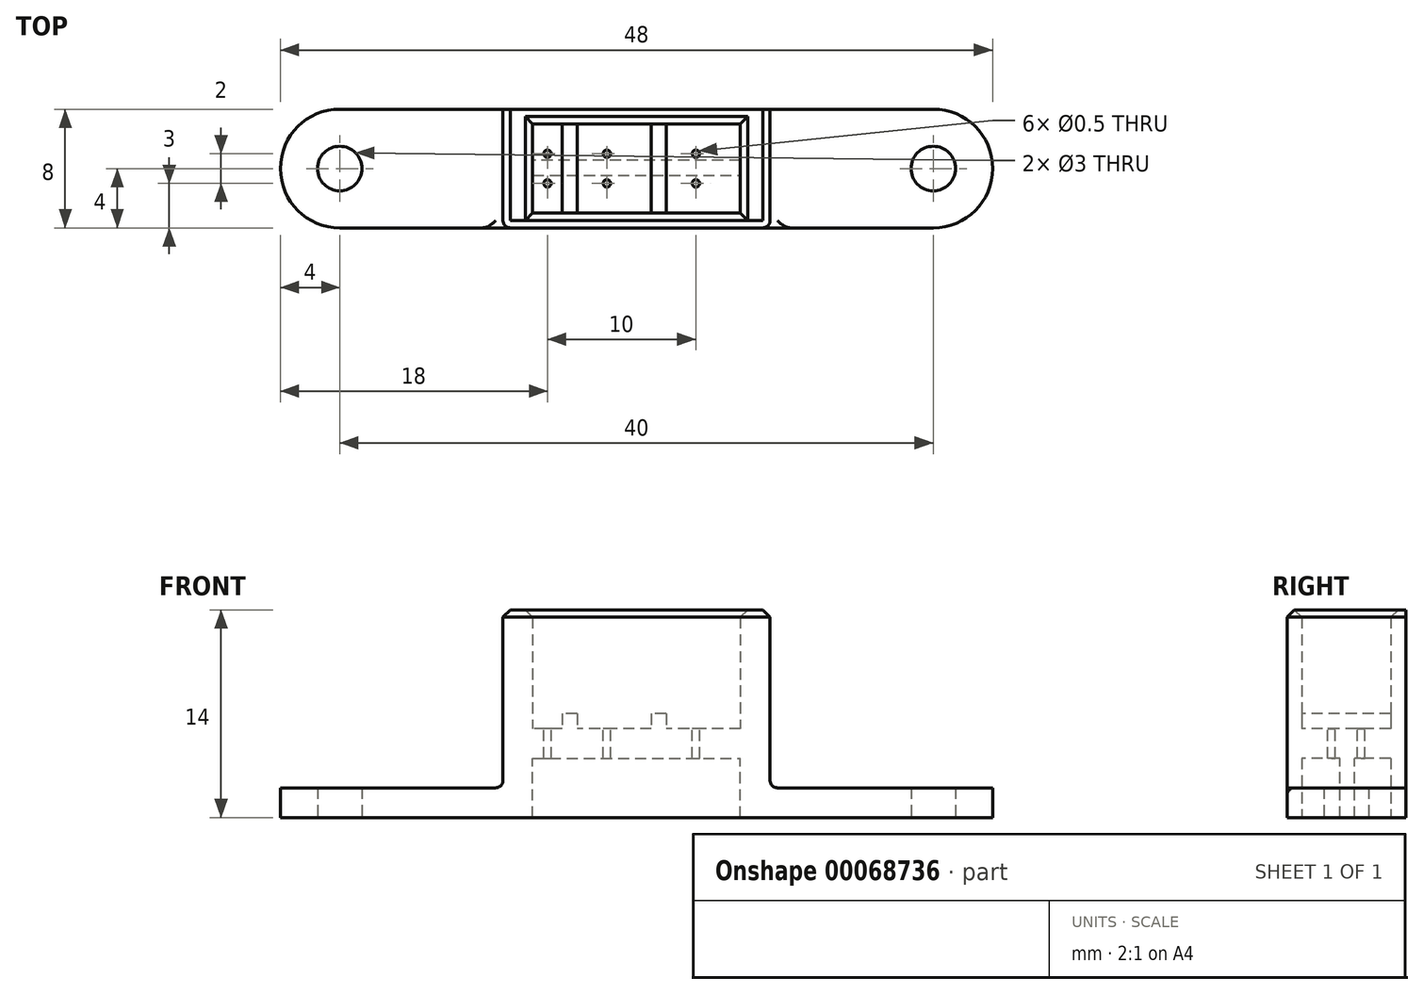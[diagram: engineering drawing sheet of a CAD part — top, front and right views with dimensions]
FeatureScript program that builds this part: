
annotation { "Feature Type Name" : "Feature", "Feature Type Description" : "" }
export const myFeature = defineFeature(function(context is Context, id is Id, definition is map)
    precondition{}
    {
        {
            var Q0;
            Q0=qCreatedBy(makeId("Top.planeOp"),FACE);
            var sketch = newSketch(context, id + "F0", { "sketchPlane" : qUnion([Q0])});
            skCircle(sketch, "E0", {"center": v(20, 0) * mm, "radius": 1.5 * mm});
            skLineSegment(sketch, "E1", {"start": v(20, 0) * mm, "end": v(0, 0) * mm, "construction": true});
            skLineSegment(sketch, "E2", {"start": v(0, 4) * mm, "end": v(20, 4) * mm});
            skLineSegment(sketch, "E3", {"start": v(0, -4) * mm, "end": v(20, -4) * mm});
            skArc(sketch, "E4", {"start": v(20, -4) * mm, "mid": v(24, 0) * mm, "end": v(20, 4) * mm});
            skLineSegment(sketch, "E5", {"start": v(0, 4) * mm, "end": v(0, -4) * mm, "construction": true});
            skLineSegment(sketch, "E6.MirrorCS", {"start": v(0, 4) * mm, "end": v(-20, 4) * mm});
            skLineSegment(sketch, "E7.MirrorCS", {"start": v(0, -4) * mm, "end": v(-20, -4) * mm});
            skArc(sketch, "E8.MirrorCS", {"start": v(-20, -4) * mm, "mid": v(-24, 0) * mm, "end": v(-20, 4) * mm});
            skCircle(sketch, "E9.MirrorC", {"center": v(-20, 0) * mm, "radius": 1.5 * mm});
            skLineSegment(sketch, "E10.MirrorCS", {"start": v(-20, 0) * mm, "end": v(0, 0) * mm, "construction": true});
            skSolve(sketch);
        }
        {
            var Q0;
            Q0 = qSketchRegion(id + "F0", true);
            extrude(context, id + "F1", {"entities" : qUnion([Q0]), "depth" : 2 * mm});
        }
        {
            var Q0;
            Q0=qCreatedBy(makeId("Top.planeOp"),FACE);
            var sketch = newSketch(context, id + "F2", { "sketchPlane" : qUnion([Q0])});
            skLineSegment(sketch, "E11.rect.bottom", {"start": v(7, -3) * mm, "end": v(-7, -3) * mm});
            skLineSegment(sketch, "E11.rect.top", {"start": v(7, 3) * mm, "end": v(-7, 3) * mm});
            skLineSegment(sketch, "E11.rect.left", {"start": v(7, -3) * mm, "end": v(7, 3) * mm});
            skLineSegment(sketch, "E11.rect.right", {"start": v(-7, -3) * mm, "end": v(-7, 3) * mm});
            skPoint(sketch, "E11.rect.middle", {"position": v(0, 0) * mm});
            skLineSegment(sketch, "E12.rect.bottom", {"start": v(9, -4) * mm, "end": v(-9, -4) * mm});
            skLineSegment(sketch, "E12.rect.top", {"start": v(9, 4) * mm, "end": v(-9, 4) * mm});
            skLineSegment(sketch, "E12.rect.left", {"start": v(9, -4) * mm, "end": v(9, 4) * mm});
            skLineSegment(sketch, "E12.rect.right", {"start": v(-9, -4) * mm, "end": v(-9, 4) * mm});
            skSolve(sketch);
        }
        {
            var Q0;
            Q0 = qSketchRegion(id + "F2", true);
            extrude(context, id + "F3", {"entities" : qUnion([Q0]), "operationType" : NewBodyOperationType.ADD, "depth" : 14 * mm});
        }
        {
            var Q0;
            Q0=makeQuery(id+"F3.boolean.opBoolean","INTERSECT",EDGE,{"derivedFrom":[makeQuery(id+"F1.opExtrude","CAP_FACE",FACE,{"disambiguationData":[OSD([sQuery(id+"F0.wireOp",EDGE,"E0"),sQuery(id+"F0.wireOp",EDGE,"E2"),sQuery(id+"F0.wireOp",EDGE,"E3"),sQuery(id+"F0.wireOp",EDGE,"E4"),sQuery(id+"F0.wireOp",EDGE,"E6.MirrorCS"),sQuery(id+"F0.wireOp",EDGE,"E7.MirrorCS"),sQuery(id+"F0.wireOp",EDGE,"E8.MirrorCS"),sQuery(id+"F0.wireOp",EDGE,"E9.MirrorC")])],"isStart":false}),makeQuery(id+"F3.opExtrude","SWEPT_FACE",FACE,{"disambiguationData":[OSD([sQuery(id+"F2.wireOp",EDGE,"E12.rect.left")])]})]});
            var Q1;
            Q1=makeQuery(id+"F3.boolean.opBoolean","INTERSECT",EDGE,{"derivedFrom":[makeQuery(id+"F1.opExtrude","CAP_FACE",FACE,{"disambiguationData":[OSD([sQuery(id+"F0.wireOp",EDGE,"E0"),sQuery(id+"F0.wireOp",EDGE,"E2"),sQuery(id+"F0.wireOp",EDGE,"E3"),sQuery(id+"F0.wireOp",EDGE,"E4"),sQuery(id+"F0.wireOp",EDGE,"E6.MirrorCS"),sQuery(id+"F0.wireOp",EDGE,"E7.MirrorCS"),sQuery(id+"F0.wireOp",EDGE,"E8.MirrorCS"),sQuery(id+"F0.wireOp",EDGE,"E9.MirrorC")])],"isStart":false}),makeQuery(id+"F3.opExtrude","SWEPT_FACE",FACE,{"disambiguationData":[OSD([sQuery(id+"F2.wireOp",EDGE,"E12.rect.right")])]})]});
            var Q2;
            Q2=makeQuery(id+"F3.opExtrude","SWEPT_EDGE",EDGE,{"disambiguationData":[OSD([sQuery(id+"F2.wireOp",EDGE,"E12.rect.bottom"),sQuery(id+"F2.wireOp",EDGE,"E12.rect.right")])]});
            var Q3;
            Q3=makeQuery(id+"F3.opExtrude","SWEPT_EDGE",EDGE,{"disambiguationData":[OSD([sQuery(id+"F2.wireOp",EDGE,"E12.rect.bottom"),sQuery(id+"F2.wireOp",EDGE,"E12.rect.left")])]});
            fillet(context, id + "F4", {"entities" : qUnion([Q0, Q1, Q2, Q3]), "radius" : 0.5 * mm, "tangentPropagation" : true, "allowEdgeOverflow" : false});
        }
        {
            var Q0;
            Q0=makeQuery(id+"F3.opExtrude","CAP_EDGE",EDGE,{"disambiguationData":[OSD([sQuery(id+"F2.wireOp",EDGE,"E11.rect.left")])],"isStart":false});
            var Q1;
            Q1=makeQuery(id+"F3.opExtrude","CAP_EDGE",EDGE,{"disambiguationData":[OSD([sQuery(id+"F2.wireOp",EDGE,"E11.rect.top")])],"isStart":false});
            var Q2;
            Q2=makeQuery(id+"F3.opExtrude","CAP_EDGE",EDGE,{"disambiguationData":[OSD([sQuery(id+"F2.wireOp",EDGE,"E11.rect.right")])],"isStart":false});
            var Q3;
            Q3=makeQuery(id+"F3.opExtrude","CAP_EDGE",EDGE,{"disambiguationData":[OSD([sQuery(id+"F2.wireOp",EDGE,"E11.rect.bottom")])],"isStart":false});
            var Q4;
            Q4=makeQuery(id+"F3.opExtrude","CAP_EDGE",EDGE,{"disambiguationData":[OSD([sQuery(id+"F2.wireOp",EDGE,"E12.rect.bottom")])],"isStart":false});
            chamfer(context, id + "F5", {"entities" : qUnion([Q0, Q1, Q2, Q3, Q4]), "width" : 0.5 * mm, "tangentPropagation" : true});
        }
        {
            var Q0;
            Q0=makeQuery(id+"F3.boolean.opBoolean","SPLIT",FACE,{"disambiguationData":[TD([makeQuery(id+"F3.opExtrude","SWEPT_FACE",FACE,{"disambiguationData":[OSD([sQuery(id+"F2.wireOp",EDGE,"E11.rect.bottom")])]})])],"derivedFrom":makeQuery(id+"F1.opExtrude","CAP_FACE",FACE,{"disambiguationData":[OSD([sQuery(id+"F0.wireOp",EDGE,"E0"),sQuery(id+"F0.wireOp",EDGE,"E2"),sQuery(id+"F0.wireOp",EDGE,"E3"),sQuery(id+"F0.wireOp",EDGE,"E4"),sQuery(id+"F0.wireOp",EDGE,"E6.MirrorCS"),sQuery(id+"F0.wireOp",EDGE,"E7.MirrorCS"),sQuery(id+"F0.wireOp",EDGE,"E8.MirrorCS"),sQuery(id+"F0.wireOp",EDGE,"E9.MirrorC")])],"isStart":false})});
            var sketch = newSketch(context, id + "F6", { "sketchPlane" : qUnion([Q0])});
            skSolve(sketch);
        }
        {
            var Q0;
            Q0 = qSketchRegion(id + "F6", true);
            var Q1;
            {var subQ0=makeQuery(id+"F1.opExtrude","CAP_FACE",FACE,{"disambiguationData":[OSD([sQuery(id+"F0.wireOp",EDGE,"E0"),sQuery(id+"F0.wireOp",EDGE,"E2"),sQuery(id+"F0.wireOp",EDGE,"E3"),sQuery(id+"F0.wireOp",EDGE,"E4"),sQuery(id+"F0.wireOp",EDGE,"E6.MirrorCS"),sQuery(id+"F0.wireOp",EDGE,"E7.MirrorCS"),sQuery(id+"F0.wireOp",EDGE,"E8.MirrorCS"),sQuery(id+"F0.wireOp",EDGE,"E9.MirrorC")])],"isStart":false});Q1=makeQuery(id+"F6.imprint","IMPRINT",FACE,{"disambiguationData":[TD([[makeQuery(id+"F6.imprint","IMPRINT",EDGE,{"derivedFrom":makeQuery(id+"F3.boolean.opBoolean","INTERSECT",EDGE,{"derivedFrom":[subQ0,makeQuery(id+"F3.opExtrude","SWEPT_FACE",FACE,{"disambiguationData":[OSD([sQuery(id+"F2.wireOp",EDGE,"E11.rect.bottom")])]})]})}),1.0]])]});}
            extrude(context, id + "F7", {"entities" : qUnion([Q0, Q1]), "operationType" : NewBodyOperationType.REMOVE, "endBound" : BoundingType.THROUGH_ALL, "oppositeDirection" : true, "depth" : 25 * mm});
        }
        {
            var Q0;
            Q0=qCreatedBy(makeId("Front.planeOp"),FACE);
            var sketch = newSketch(context, id + "F8", { "sketchPlane" : qUnion([Q0])});
            skLineSegment(sketch, "E13.bottom", {"start": v(-8.5, 4) * mm, "end": v(8.5, 4) * mm});
            skLineSegment(sketch, "E13.top", {"start": v(-8.5, 6) * mm, "end": v(8.5, 6) * mm});
            skLineSegment(sketch, "E13.left", {"start": v(-8.5, 4) * mm, "end": v(-8.5, 6) * mm});
            skLineSegment(sketch, "E13.right", {"start": v(8.5, 4) * mm, "end": v(8.5, 6) * mm});
            skLineSegment(sketch, "E14", {"start": v(0, 0) * mm, "end": v(0, 4) * mm, "construction": true});
            skSolve(sketch);
        }
        {
            var Q0;
            Q0 = qSketchRegion(id + "F8", true);
            var Q1;
            {var subQ0=sQuery(id+"F2.wireOp",EDGE,"E11.rect.top");Q1=makeQuery(id+"F7.boolean.opBoolean","MERGE",FACE,{"derivedFrom":[makeQuery(id+"F3.opExtrude","SWEPT_FACE",FACE,{"disambiguationData":[OSD([subQ0])]}),makeQuery(id+"F7.opExtrude","SWEPT_FACE",FACE,{"disambiguationData":[OSD([sQuery(id+"F0.wireOp",EDGE,"E0"),sQuery(id+"F0.wireOp",EDGE,"E2"),sQuery(id+"F0.wireOp",EDGE,"E3"),sQuery(id+"F0.wireOp",EDGE,"E4"),sQuery(id+"F0.wireOp",EDGE,"E6.MirrorCS"),sQuery(id+"F0.wireOp",EDGE,"E7.MirrorCS"),sQuery(id+"F0.wireOp",EDGE,"E8.MirrorCS"),sQuery(id+"F0.wireOp",EDGE,"E9.MirrorC"),subQ0])]})]});}
            var Q2;
            {var subQ0=sQuery(id+"F2.wireOp",EDGE,"E11.rect.bottom");Q2=makeQuery(id+"F7.boolean.opBoolean","MERGE",FACE,{"derivedFrom":[makeQuery(id+"F3.opExtrude","SWEPT_FACE",FACE,{"disambiguationData":[OSD([subQ0])]}),makeQuery(id+"F7.opExtrude","SWEPT_FACE",FACE,{"disambiguationData":[OSD([sQuery(id+"F0.wireOp",EDGE,"E0"),sQuery(id+"F0.wireOp",EDGE,"E2"),sQuery(id+"F0.wireOp",EDGE,"E3"),sQuery(id+"F0.wireOp",EDGE,"E4"),sQuery(id+"F0.wireOp",EDGE,"E6.MirrorCS"),sQuery(id+"F0.wireOp",EDGE,"E7.MirrorCS"),sQuery(id+"F0.wireOp",EDGE,"E8.MirrorCS"),sQuery(id+"F0.wireOp",EDGE,"E9.MirrorC"),subQ0])]})]});}
            extrude(context, id + "F9", {"entities" : qUnion([Q0]), "operationType" : NewBodyOperationType.ADD, "endBound" : BoundingType.UP_TO_SURFACE, "oppositeDirection" : true, "endBoundEntityFace" : qUnion([Q1]), "depth" : 25 * mm, "hasSecondDirection" : true, "secondDirectionBound" : SecondDirectionBoundingType.UP_TO_SURFACE, "secondDirectionOppositeDirection" : false, "secondDirectionBoundEntityFace" : qUnion([Q2]), "secondDirectionDepth" : 25 * mm});
        }
        {
            var Q0;
            Q0=makeQuery(id+"F9.opExtrude","SWEPT_FACE",FACE,{"disambiguationData":[OSD([sQuery(id+"F8.wireOp",EDGE,"E13.top")])]});
            var sketch = newSketch(context, id + "F10", { "sketchPlane" : qUnion([Q0])});
            skLineSegment(sketch, "E15.bottom", {"start": v(1, 3) * mm, "end": v(2, 3) * mm});
            skLineSegment(sketch, "E15.top", {"start": v(1, -3) * mm, "end": v(2, -3) * mm});
            skLineSegment(sketch, "E15.left", {"start": v(1, 3) * mm, "end": v(1, -3) * mm});
            skLineSegment(sketch, "E15.right", {"start": v(2, 3) * mm, "end": v(2, -3) * mm});
            skLineSegment(sketch, "E16.bottom", {"start": v(-5, 3) * mm, "end": v(-4, 3) * mm});
            skLineSegment(sketch, "E16.top", {"start": v(-5, -3) * mm, "end": v(-4, -3) * mm});
            skLineSegment(sketch, "E16.left", {"start": v(-5, 3) * mm, "end": v(-5, -3) * mm});
            skLineSegment(sketch, "E16.right", {"start": v(-4, 3) * mm, "end": v(-4, -3) * mm});
            skSolve(sketch);
        }
        {
            var Q0;
            Q0 = qSketchRegion(id + "F10", true);
            extrude(context, id + "F11", {"entities" : qUnion([Q0]), "operationType" : NewBodyOperationType.ADD, "depth" : 1 * mm});
        }
        {
            var Q0;
            Q0=makeQuery(id+"F11.boolean.opBoolean","SPLIT",FACE,{"disambiguationData":[TD([makeQuery(id+"F11.opExtrude","SWEPT_FACE",FACE,{"disambiguationData":[OSD([sQuery(id+"F10.wireOp",EDGE,"E15.left")])]})])],"derivedFrom":makeQuery(id+"F9.opExtrude","SWEPT_FACE",FACE,{"disambiguationData":[OSD([sQuery(id+"F8.wireOp",EDGE,"E13.top")])]})});
            var sketch = newSketch(context, id + "F12", { "sketchPlane" : qUnion([Q0])});
            skLineSegment(sketch, "E17", {"start": v(-7, 0) * mm, "end": v(7, 0) * mm, "construction": true});
            skPoint(sketch, "E17.startSnap0", {"position": v(-4, 0) * mm});
            skPoint(sketch, "E17.endSnap0", {"position": v(1, 0) * mm});
            skCircle(sketch, "E18", {"center": v(-2, 1) * mm, "radius": 0.25 * mm});
            skCircle(sketch, "E19", {"center": v(-2, -1) * mm, "radius": 0.25 * mm});
            skLineSegment(sketch, "E20", {"start": v(-2, 1) * mm, "end": v(-2, -1) * mm, "construction": true});
            skLineSegment(sketch, "E21", {"start": v(4, 1) * mm, "end": v(4, -1) * mm, "construction": true});
            skCircle(sketch, "E22", {"center": v(4, 1) * mm, "radius": 0.25 * mm});
            skCircle(sketch, "E23", {"center": v(4, -1) * mm, "radius": 0.25 * mm});
            skCircle(sketch, "E24", {"center": v(-6, 1) * mm, "radius": 0.25 * mm});
            skLineSegment(sketch, "E25", {"start": v(-6, 1) * mm, "end": v(-6, -1) * mm, "construction": true});
            skCircle(sketch, "E26", {"center": v(-6, -1) * mm, "radius": 0.25 * mm});
            skSolve(sketch);
        }
        {
            var Q0;
            Q0 = qSketchRegion(id + "F12", true);
            extrude(context, id + "F13", {"entities" : qUnion([Q0]), "operationType" : NewBodyOperationType.REMOVE, "endBound" : BoundingType.THROUGH_ALL, "oppositeDirection" : true, "depth" : 25 * mm});
        }
        {
            var Q0;
            Q0=makeQuery(id+"F9.opExtrude","SWEPT_FACE",FACE,{"disambiguationData":[OSD([sQuery(id+"F8.wireOp",EDGE,"E13.bottom")])]});
            var sketch = newSketch(context, id + "F14", { "sketchPlane" : qUnion([Q0])});
            skLineSegment(sketch, "E27.bottom", {"start": v(-7, 0.44) * mm, "end": v(7, 0.44) * mm});
            skLineSegment(sketch, "E27.top", {"start": v(-7, -0.56) * mm, "end": v(7, -0.56) * mm});
            skLineSegment(sketch, "E27.left", {"start": v(-7, 0.44) * mm, "end": v(-7, -0.56) * mm});
            skLineSegment(sketch, "E27.right", {"start": v(7, 0.44) * mm, "end": v(7, -0.56) * mm});
            skLineSegment(sketch, "E28", {"start": v(-7, -0.06) * mm, "end": v(7, -0.06) * mm, "construction": true});
            skSolve(sketch);
        }
        {
            var Q0;
            Q0 = qSketchRegion(id + "F14", true);
            var Q1;
            Q1=makeQuery(id+"F1.opExtrude","CAP_FACE",FACE,{"disambiguationData":[OSD([sQuery(id+"F0.wireOp",EDGE,"E0"),sQuery(id+"F0.wireOp",EDGE,"E2"),sQuery(id+"F0.wireOp",EDGE,"E3"),sQuery(id+"F0.wireOp",EDGE,"E4"),sQuery(id+"F0.wireOp",EDGE,"E6.MirrorCS"),sQuery(id+"F0.wireOp",EDGE,"E7.MirrorCS"),sQuery(id+"F0.wireOp",EDGE,"E8.MirrorCS"),sQuery(id+"F0.wireOp",EDGE,"E9.MirrorC")])],"isStart":true});
            extrude(context, id + "F15", {"entities" : qUnion([Q0]), "operationType" : NewBodyOperationType.ADD, "endBound" : BoundingType.UP_TO_SURFACE, "endBoundEntityFace" : qUnion([Q1]), "depth" : 25 * mm});
        }
    });
